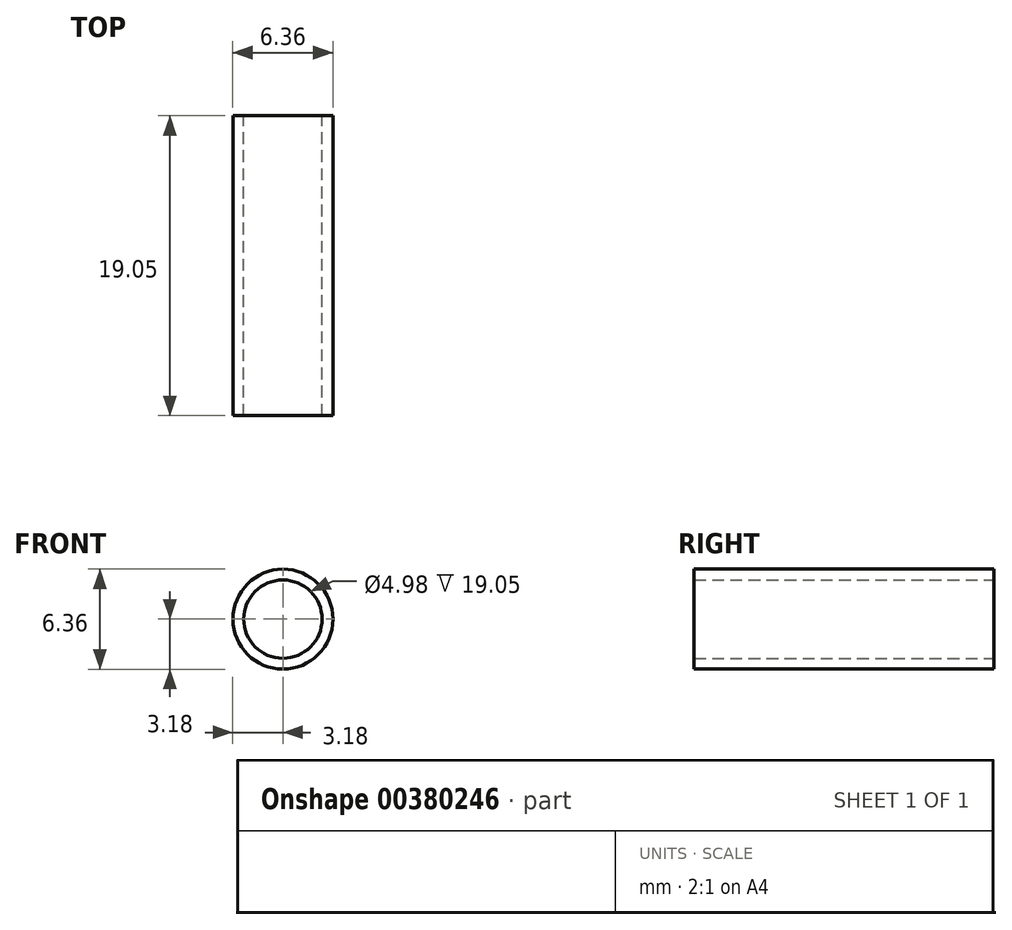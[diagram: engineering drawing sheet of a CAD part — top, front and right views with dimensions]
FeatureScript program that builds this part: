
annotation { "Feature Type Name" : "Feature", "Feature Type Description" : "" }
export const myFeature = defineFeature(function(context is Context, id is Id, definition is map)
    precondition{}
    {
        {
            var Q0;
            Q0=qCreatedBy(makeId("Front.planeOp"),FACE);
            var sketch = newSketch(context, id + "F0", { "sketchPlane" : qUnion([Q0])});
            skCircle(sketch, "E0", {"center": v(0, 0) * mm, "radius": 3.18 * mm});
            skCircle(sketch, "E1", {"center": v(0, 0) * mm, "radius": 2.49 * mm});
            skSolve(sketch);
        }
        {
            var Q0;
            Q0 = qSketchRegion(id + "F0", true);
            extrude(context, id + "F1", {"entities" : qUnion([Q0]), "depth" : 19.05 * mm});
        }
    });
